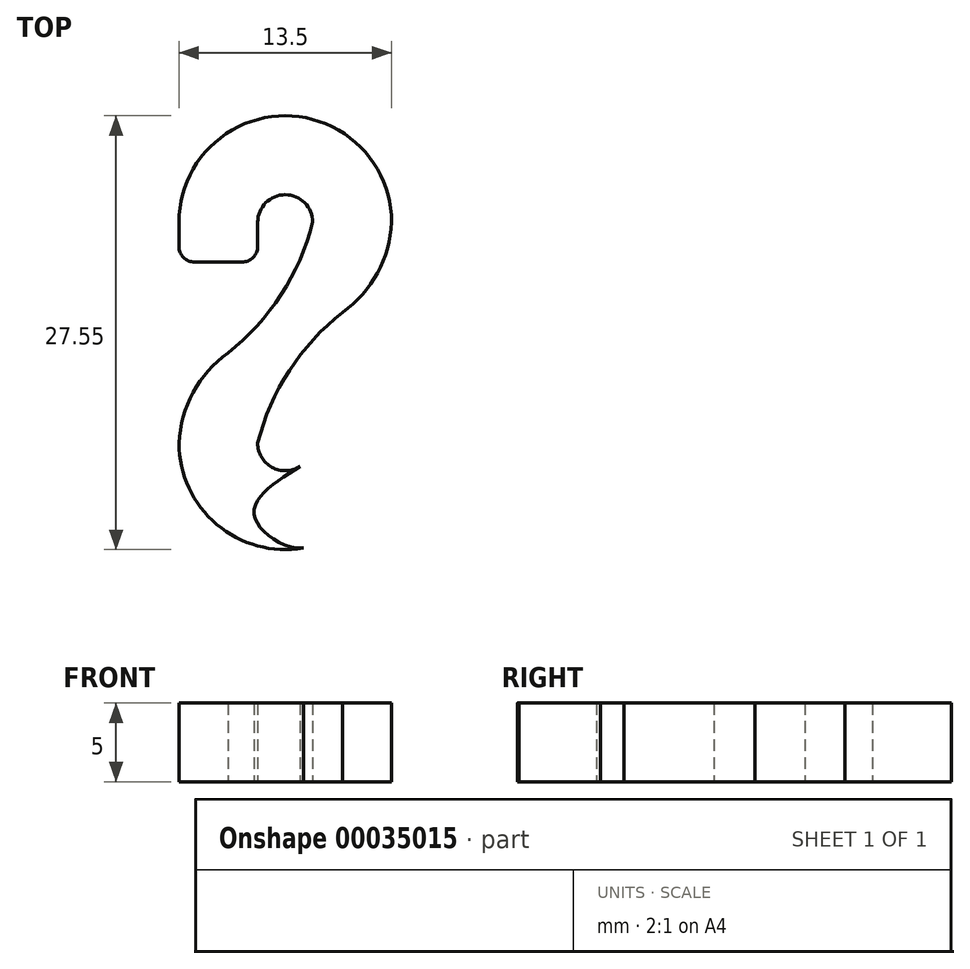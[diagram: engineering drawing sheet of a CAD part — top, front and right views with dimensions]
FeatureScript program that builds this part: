
annotation { "Feature Type Name" : "Feature", "Feature Type Description" : "" }
export const myFeature = defineFeature(function(context is Context, id is Id, definition is map)
    precondition{}
    {
        {
            var Q0;
            Q0=qCreatedBy(makeId("Top.planeOp"),FACE);
            var sketch = newSketch(context, id + "F0", { "sketchPlane" : qUnion([Q0])});
            skLineSegment(sketch, "E0", {"start": v(0.24, 11.49) * mm, "end": v(0.24, 13.86) * mm, "construction": true});
            skArc(sketch, "E1", {"start": v(6.99, 8.63) * mm, "mid": v(0.24, 15.39) * mm, "end": v(-6.51, 8.63) * mm});
            skLineSegment(sketch, "E2", {"start": v(4, 1.61) * mm, "end": v(-3.29, 1.61) * mm, "construction": true});
            skLineSegment(sketch, "E3.MirrorCS", {"start": v(0.24, -8.26) * mm, "end": v(0.24, -10.63) * mm, "construction": true});
            skArc(sketch, "E4", {"start": v(-3.4, 0.32) * mm, "mid": v(-5.61, -2.18) * mm, "end": v(-6.51, -5.4) * mm});
            skArc(sketch, "E5.MirrorCS", {"start": v(3.88, 2.9) * mm, "mid": v(6.1, 5.4) * mm, "end": v(6.99, 8.63) * mm});
            skArc(sketch, "E6", {"start": v(-3.4, 0.32) * mm, "mid": v(-0.02, 4.03) * mm, "end": v(1.99, 8.63) * mm});
            skArc(sketch, "E7.MirrorCS", {"start": v(3.88, 2.9) * mm, "mid": v(0.5, -0.8) * mm, "end": v(-1.51, -5.4) * mm});
            skArc(sketch, "E8", {"start": v(-1.51, 8.63) * mm, "mid": v(0.24, 6.88) * mm, "end": v(1.99, 8.63) * mm, "construction": true});
            skArc(sketch, "E9", {"start": v(1.99, 8.63) * mm, "mid": v(0.24, 10.38) * mm, "end": v(-1.51, 8.63) * mm});
            skArc(sketch, "E10", {"start": v(-1.51, -5.4) * mm, "mid": v(0.24, -3.65) * mm, "end": v(1.99, -5.4) * mm, "construction": true});
            skArc(sketch, "E11", {"start": v(1.99, -5.4) * mm, "mid": v(0.24, -7.15) * mm, "end": v(-1.51, -5.4) * mm});
            skLineSegment(sketch, "E12.MirrorCS", {"start": v(-1.51, 8.63) * mm, "end": v(-1.51, 6.1) * mm});
            skLineSegment(sketch, "E13.MirrorCS", {"start": v(-1.51, 6.1) * mm, "end": v(-6.51, 6.1) * mm});
            skLineSegment(sketch, "E14.MirrorCS", {"start": v(-6.51, 8.63) * mm, "end": v(-6.51, 6.1) * mm});
            skFitSpline(sketch, "E15", {"points": [v(1.24, -6.84) * mm, v(4.45, -4.15) * mm, v(6.73, -1.37) * mm, v(8.63, 0) * mm, v(10.52, -0.98) * mm, v(9.13, -4.04) * mm, v(6.54, -7.85) * mm, v(1.4, -12.06) * mm, v(-1.74, -9.78) * mm, v(1.24, -6.84) * mm]});
            skArc(sketch, "E16", {"start": v(1.4, -12.06) * mm, "mid": v(-4.11, -10.57) * mm, "end": v(-6.51, -5.4) * mm});
            skSolve(sketch);
        }
        {
            var Q0;
            Q0=makeQuery(id+"F0.imprint","IMPRINT",FACE,{"disambiguationData":[TD([[makeQuery(id+"F0.imprint","IMPRINT",EDGE,{"derivedFrom":sQuery(id+"F0.wireOp",EDGE,"E1")}),1.0]])]});
            extrude(context, id + "F1", {"entities" : qUnion([Q0]), "depth" : 5 * mm});
        }
        {
            var Q0;
            Q0=makeQuery(id+"F1.opExtrude","SWEPT_EDGE",EDGE,{"disambiguationData":[OSD([sQuery(id+"F0.wireOp",EDGE,"E12.MirrorCS"),sQuery(id+"F0.wireOp",EDGE,"E13.MirrorCS")])]});
            var Q1;
            Q1=makeQuery(id+"F1.opExtrude","SWEPT_EDGE",EDGE,{"disambiguationData":[OSD([sQuery(id+"F0.wireOp",EDGE,"E13.MirrorCS"),sQuery(id+"F0.wireOp",EDGE,"E14.MirrorCS")])]});
            fillet(context, id + "F2", {"entities" : qUnion([Q0, Q1]), "radius" : 1 * mm, "tangentPropagation" : true, "allowEdgeOverflow" : false});
        }
    });
